# Revit family: QF_ELECTROLUXPROFESSIONAL_1LSNLD_IC64821R_E
name_source: partatom
category: Attrezzature speciali
units: mm (PartAtom-declared; Revit-internal decimal feet)

## family parameters
Basato su piano di lavoro = No
Condiviso = No
Punto di calcolo locali = No
Quota connettore circolare = Usa diametro
Sempre verticale = Sì
Taglio con vuoti quando caricato = No
Tipo di parte = Normale

## types (1)
- 9882030285
    Cycle = 50 Hz
    Depth Actual = 1620 mm
    Descrizione = IRONER CYLINDER IC64821R REAR DELIVERY 2120MM SUPERIOR EL. CE 400/50/3 DUBIXIUM ML FEED ALONE VAC.FEED.TABLE
    Gas KW = 0
    Height Actual = 1270 mm  [stored 4.16667 ft]
    Item Number = 1L0H8Y
    Latent Heat Output = 0.0
    Length Actual = 2785 mm  [stored 9.13714 ft]
    Modello = IC64821R
    Phase = 3
    Produttore = Electrolux Professional
    Prospetto di default = 0 mm  [stored 0 ft]
    Sensible Heat Output = 0.0
    Steam Pounds per Hour = 0
    URL = www.electroluxprofessional.com
    Volts = 400 V
    Watts = 37700 W
    Weight = 940

note: [stored X ft] marks values corroborated as IEEE doubles in the binary element streams (Revit-internal decimal feet)

## geometry (parser evidence)
native form markers: Sweep x10
no freeform markers — native parametric forms only
